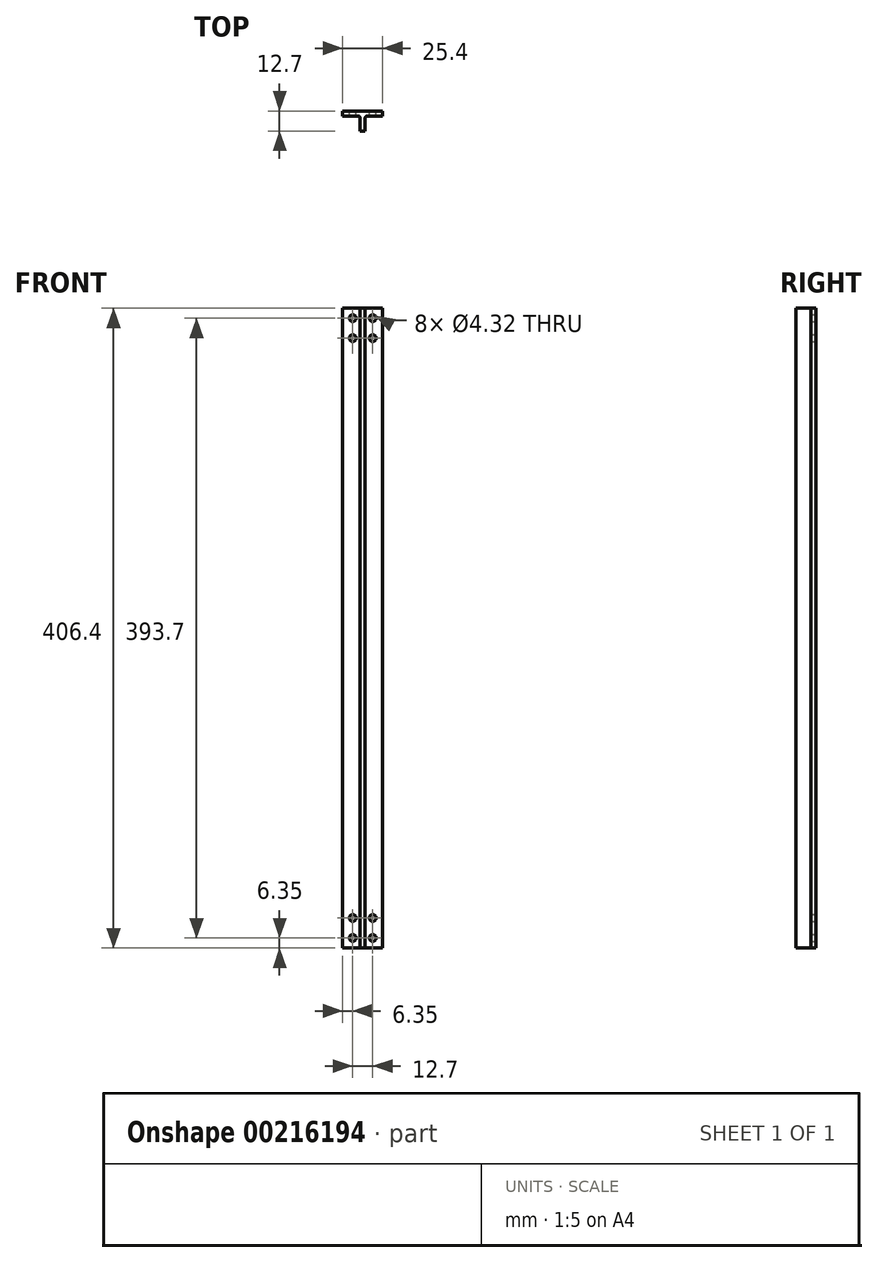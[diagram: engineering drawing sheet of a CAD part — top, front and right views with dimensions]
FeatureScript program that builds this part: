
annotation { "Feature Type Name" : "Feature", "Feature Type Description" : "" }
export const myFeature = defineFeature(function(context is Context, id is Id, definition is map)
    precondition{}
    {
        {
            var Q0;
            Q0=qCreatedBy(makeId("Top.planeOp"),FACE);
            var sketch = newSketch(context, id + "F0", { "sketchPlane" : qUnion([Q0])});
            skLineSegment(sketch, "E0", {"start": v(0, 0) * mm, "end": v(12.7, 0) * mm});
            skLineSegment(sketch, "E1", {"start": v(12.7, 0) * mm, "end": v(12.7, -3.18) * mm});
            skLineSegment(sketch, "E2", {"start": v(12.7, -3.18) * mm, "end": v(1.59, -3.18) * mm});
            skLineSegment(sketch, "E3", {"start": v(1.59, -3.18) * mm, "end": v(1.59, -12.7) * mm});
            skLineSegment(sketch, "E4", {"start": v(1.59, -12.7) * mm, "end": v(0, -12.7) * mm});
            skLineSegment(sketch, "E5.MirrorCS", {"start": v(-1.59, -12.7) * mm, "end": v(0, -12.7) * mm});
            skLineSegment(sketch, "E6.MirrorCS", {"start": v(-12.7, -3.18) * mm, "end": v(-1.59, -3.18) * mm});
            skLineSegment(sketch, "E7.MirrorCS", {"start": v(-1.59, -3.18) * mm, "end": v(-1.59, -12.7) * mm});
            skLineSegment(sketch, "E8.MirrorCS", {"start": v(0, 0) * mm, "end": v(-12.7, 0) * mm});
            skLineSegment(sketch, "E9.MirrorCS", {"start": v(-12.7, 0) * mm, "end": v(-12.7, -3.18) * mm});
            skSolve(sketch);
        }
        {
            var Q0;
            Q0 = qSketchRegion(id + "F0", true);
            extrude(context, id + "F1", {"entities" : qUnion([Q0]), "depth" : 406.4 * mm});
        }
        {
            var Q0;
            Q0=makeQuery(id+"F1.opExtrude","SWEPT_EDGE",EDGE,{"disambiguationData":[OSD([sQuery(id+"F0.wireOp",EDGE,"E6.MirrorCS"),sQuery(id+"F0.wireOp",EDGE,"E7.MirrorCS")])]});
            var Q1;
            Q1=makeQuery(id+"F1.opExtrude","SWEPT_EDGE",EDGE,{"disambiguationData":[OSD([sQuery(id+"F0.wireOp",EDGE,"E2"),sQuery(id+"F0.wireOp",EDGE,"E3")])]});
            fillet(context, id + "F2", {"entities" : qUnion([Q0, Q1]), "radius" : 1.27 * mm, "tangentPropagation" : true, "allowEdgeOverflow" : false});
        }
        {
            var Q0;
            Q0=makeQuery(id+"F1.opExtrude","SWEPT_FACE",FACE,{"disambiguationData":[OSD([sQuery(id+"F0.wireOp",EDGE,"E0"),sQuery(id+"F0.wireOp",EDGE,"E8.MirrorCS")])]});
            var sketch = newSketch(context, id + "F3", { "sketchPlane" : qUnion([Q0])});
            skLineSegment(sketch, "E10", {"start": v(-12.7, 406.4) * mm, "end": v(0, 406.4) * mm});
            skLineSegment(sketch, "E11", {"start": v(0, 406.4) * mm, "end": v(0, 400.05) * mm});
            skLineSegment(sketch, "E12", {"start": v(0, 400.05) * mm, "end": v(0, 387.35) * mm});
            skLineSegment(sketch, "E13", {"start": v(0, 387.35) * mm, "end": v(-12.7, 387.35) * mm});
            skLineSegment(sketch, "E14", {"start": v(-12.7, 387.35) * mm, "end": v(-6.35, 387.35) * mm});
            skLineSegment(sketch, "E15", {"start": v(-6.35, 387.35) * mm, "end": v(-6.35, 400.05) * mm});
            skLineSegment(sketch, "E16.MirrorCS", {"start": v(6.35, 387.35) * mm, "end": v(6.35, 400.05) * mm});
            skLineSegment(sketch, "E17", {"start": v(-12.7, 203.2) * mm, "end": v(12.7, 203.2) * mm});
            skLineSegment(sketch, "E18.MirrorCS", {"start": v(-6.35, 19.05) * mm, "end": v(-6.35, 6.35) * mm});
            skLineSegment(sketch, "E19.MirrorCS", {"start": v(0, 19.05) * mm, "end": v(-12.7, 19.05) * mm});
            skLineSegment(sketch, "E20.MirrorCS", {"start": v(0, 6.35) * mm, "end": v(0, 19.05) * mm});
            skLineSegment(sketch, "E21.MirrorCS", {"start": v(-12.7, 19.05) * mm, "end": v(-6.35, 19.05) * mm});
            skLineSegment(sketch, "E22.MirrorCS", {"start": v(0, 0) * mm, "end": v(0, 6.35) * mm});
            skLineSegment(sketch, "E23.MirrorCS", {"start": v(6.35, 19.05) * mm, "end": v(6.35, 6.35) * mm});
            skLineSegment(sketch, "E24.MirrorCS", {"start": v(-12.7, 0) * mm, "end": v(0, 0) * mm});
            skSolve(sketch);
        }
        {
            var Q0;
            Q0=sQuery(id+"F3.wireOp",VERTEX,"E15.end");
            var Q1;
            Q1=sQuery(id+"F3.wireOp",VERTEX,"E15.start");
            var Q2;
            Q2=sQuery(id+"F3.wireOp",VERTEX,"E16.MirrorCS.start");
            var Q3;
            Q3=sQuery(id+"F3.wireOp",VERTEX,"E16.MirrorCS.end");
            var Q4;
            Q4=sQuery(id+"F3.wireOp",VERTEX,"E18.MirrorCS.end");
            var Q5;
            Q5=sQuery(id+"F3.wireOp",VERTEX,"E21.MirrorCS.end");
            var Q6;
            Q6=sQuery(id+"F3.wireOp",VERTEX,"E23.MirrorCS.start");
            var Q7;
            Q7=sQuery(id+"F3.wireOp",VERTEX,"E23.MirrorCS.end");
            var Q8;
            Q8=makeQuery(id+"F1.opExtrude","SWEPT_BODY",BODY,{"disambiguationData":[OSD([sQuery(id+"F0.wireOp",EDGE,"E0"),sQuery(id+"F0.wireOp",EDGE,"E1"),sQuery(id+"F0.wireOp",EDGE,"E2"),sQuery(id+"F0.wireOp",EDGE,"E3"),sQuery(id+"F0.wireOp",EDGE,"E4"),sQuery(id+"F0.wireOp",EDGE,"E5.MirrorCS"),sQuery(id+"F0.wireOp",EDGE,"E6.MirrorCS"),sQuery(id+"F0.wireOp",EDGE,"E7.MirrorCS"),sQuery(id+"F0.wireOp",EDGE,"E8.MirrorCS"),sQuery(id+"F0.wireOp",EDGE,"E9.MirrorCS")])]});
            hole(context, id + "F4", {"style" : HoleStyle.SIMPLE, "endStyle" : HoleEndStyle.BLIND, "standardTappedOrClearance" : lookupTablePath({ "standard" : "ANSI", "fit" : "Close", "size" : "#8", "type" : "Clearance" }), "standardBlindInLast" : lookupTablePath({ "fit" : "Close", "standard" : "ANSI", "size" : "#8", "type" : "Clearance" }), "holeDiameter" : 4.32 * mm, "holeDepth" : 25.4 * mm, "locations" : qUnion([Q0, Q1, Q2, Q3, Q4, Q5, Q6, Q7]), "scope" : qUnion([Q8])});
        }
    });
